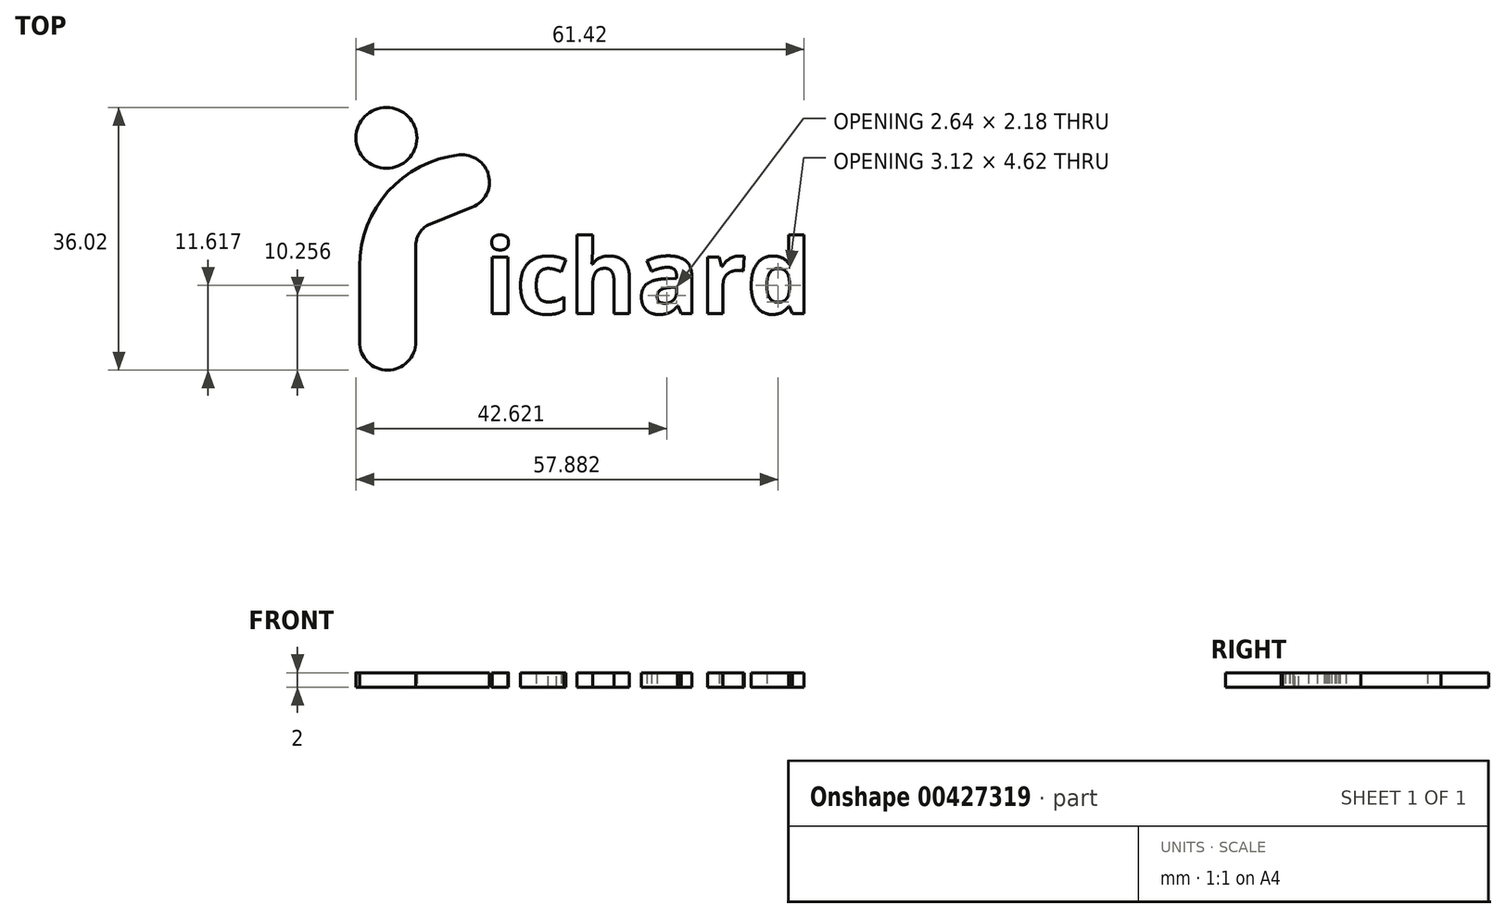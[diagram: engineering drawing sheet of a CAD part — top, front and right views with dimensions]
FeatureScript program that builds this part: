
annotation { "Feature Type Name" : "Feature", "Feature Type Description" : "" }
export const myFeature = defineFeature(function(context is Context, id is Id, definition is map)
    precondition{}
    {
        {
            var Q0;
            Q0=qCreatedBy(makeId("Top.planeOp"),FACE);
            var sketch = newSketch(context, id + "F0", { "sketchPlane" : qUnion([Q0])});
            skLineSegment(sketch, "E0", {"start": v(1.26, 2.1) * mm, "end": v(1.26, 12.49) * mm});
            skLineSegment(sketch, "E1", {"start": v(9, 2.1) * mm, "end": v(9, 15.36) * mm});
            skLineSegment(sketch, "E2", {"start": v(10.94, 18.24) * mm, "end": v(16.74, 20.58) * mm});
            skArc(sketch, "E3", {"start": v(14.96, 27.73) * mm, "mid": v(5.2, 22.73) * mm, "end": v(1.26, 12.49) * mm});
            skArc(sketch, "E4", {"start": v(10.94, 18.24) * mm, "mid": v(9.52, 17.1) * mm, "end": v(9, 15.36) * mm});
            skArc(sketch, "E5", {"start": v(16.74, 20.58) * mm, "mid": v(18.96, 24.93) * mm, "end": v(14.96, 27.73) * mm});
            skArc(sketch, "E6", {"start": v(1.26, 2.1) * mm, "mid": v(5.13, -1.77) * mm, "end": v(9, 2.1) * mm});
            skCircle(sketch, "E7", {"center": v(4.96, 30.07) * mm, "radius": 4.18 * mm});
            skText(sketch, "E8", { "text": "ichard", "fontName": "OpenSans-Bold.ttf"});
            const initialGuessF0  = {"E8": [0.01837, 0.00599, 1, 0, 0.01021]};
            skSetInitialGuess(sketch, initialGuessF0);
            skSolve(sketch);
        }
        {
            var Q0;
            Q0=makeQuery(id+"F0.imprint","IMPRINT",FACE,{"disambiguationData":[TD([[makeQuery(id+"F0.imprint","IMPRINT",EDGE,{"derivedFrom":sQuery(id+"F0.wireOp",EDGE,"E0")}),-1.0]])]});
            var Q1;
            Q1=makeQuery(id+"F0.imprint","IMPRINT",FACE,{"disambiguationData":[TD([[makeQuery(id+"F0.imprint","IMPRINT",EDGE,{"derivedFrom":sQuery(id+"F0.wireOp",EDGE,"E7")}),1.0]])]});
            var Q2;
            Q2=makeQuery(id+"F0.imprint","IMPRINT",FACE,{"disambiguationData":[TD([[makeQuery(id+"F0.imprint","IMPRINT",EDGE,{"derivedFrom":sQuery(id+"F0.wireOp",EDGE,"E8.sketch_text.stroke-0")}),-1.0]])]});
            var Q3;
            Q3=makeQuery(id+"F0.imprint","IMPRINT",FACE,{"disambiguationData":[TD([[makeQuery(id+"F0.imprint","IMPRINT",EDGE,{"derivedFrom":sQuery(id+"F0.wireOp",EDGE,"E8.sketch_text.stroke-5")}),-1.0]])]});
            var Q4;
            Q4=makeQuery(id+"F0.imprint","IMPRINT",FACE,{"disambiguationData":[TD([[makeQuery(id+"F0.imprint","IMPRINT",EDGE,{"derivedFrom":sQuery(id+"F0.wireOp",EDGE,"E8.sketch_text.stroke-9")}),-1.0]])]});
            var Q5;
            Q5=makeQuery(id+"F0.imprint","IMPRINT",FACE,{"disambiguationData":[TD([[makeQuery(id+"F0.imprint","IMPRINT",EDGE,{"derivedFrom":sQuery(id+"F0.wireOp",EDGE,"E8.sketch_text.stroke-23")}),-1.0]])]});
            var Q6;
            Q6=makeQuery(id+"F0.imprint","IMPRINT",FACE,{"disambiguationData":[TD([[makeQuery(id+"F0.imprint","IMPRINT",EDGE,{"derivedFrom":sQuery(id+"F0.wireOp",EDGE,"E8.sketch_text.stroke-65")}),-1.0]])]});
            var Q7;
            Q7=makeQuery(id+"F0.imprint","IMPRINT",FACE,{"disambiguationData":[TD([[makeQuery(id+"F0.imprint","IMPRINT",EDGE,{"derivedFrom":sQuery(id+"F0.wireOp",EDGE,"E8.sketch_text.stroke-40")}),-1.0]])]});
            var Q8;
            Q8=makeQuery(id+"F0.imprint","IMPRINT",FACE,{"disambiguationData":[TD([[makeQuery(id+"F0.imprint","IMPRINT",EDGE,{"derivedFrom":sQuery(id+"F0.wireOp",EDGE,"E8.sketch_text.stroke-78")}),-1.0]])]});
            extrude(context, id + "F1", {"entities" : qUnion([Q0, Q1, Q2, Q3, Q4, Q5, Q6, Q7, Q8]), "depth" : 2 * mm, "offsetDistance" : 25 * mm});
        }
    });
